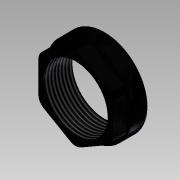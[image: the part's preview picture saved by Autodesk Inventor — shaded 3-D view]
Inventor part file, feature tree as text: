
AUTODESK INVENTOR PART (.ipt)
format: ipt  version: 2015 SP1 (Build 190203100, 203)  size: 118,784 bytes
history: native  units: mm
features: extrude x2, sketch x2, thread x1, fillet x1
ambient origin geometry x8: Origin, YZ Plane, XZ Plane, XY Plane, X Axis, Y Axis, Z Axis, Center Point
bodies: Solid1 (feature_tree)
feature tree (6):
  extrude  "Extrusion1"  Depth=4.45mm
  thread  "Thread1"  [1 undecoded]
  extrude  "Extrusion2"  Depth=3.81mm TaperAngle=0.0deg
  fillet  "Fillet1"  Radius=3.0mm
  sketch  "Sketch1"  dims[d0=18.4mm d1=3.15mm d2=4.45mm d3=0.0mm]
  sketch  "Sketch2"  dims[d4=10.0mm d5=0.0mm d6=3.81mm d7=0.0mm d8=3.0mm d9=24.7mm]
note: 1 required parameter value undecoded (feature->parameter linkage not recoverable at this tier; creation-order binding heuristic only, values carry confidence <= 0.55)
